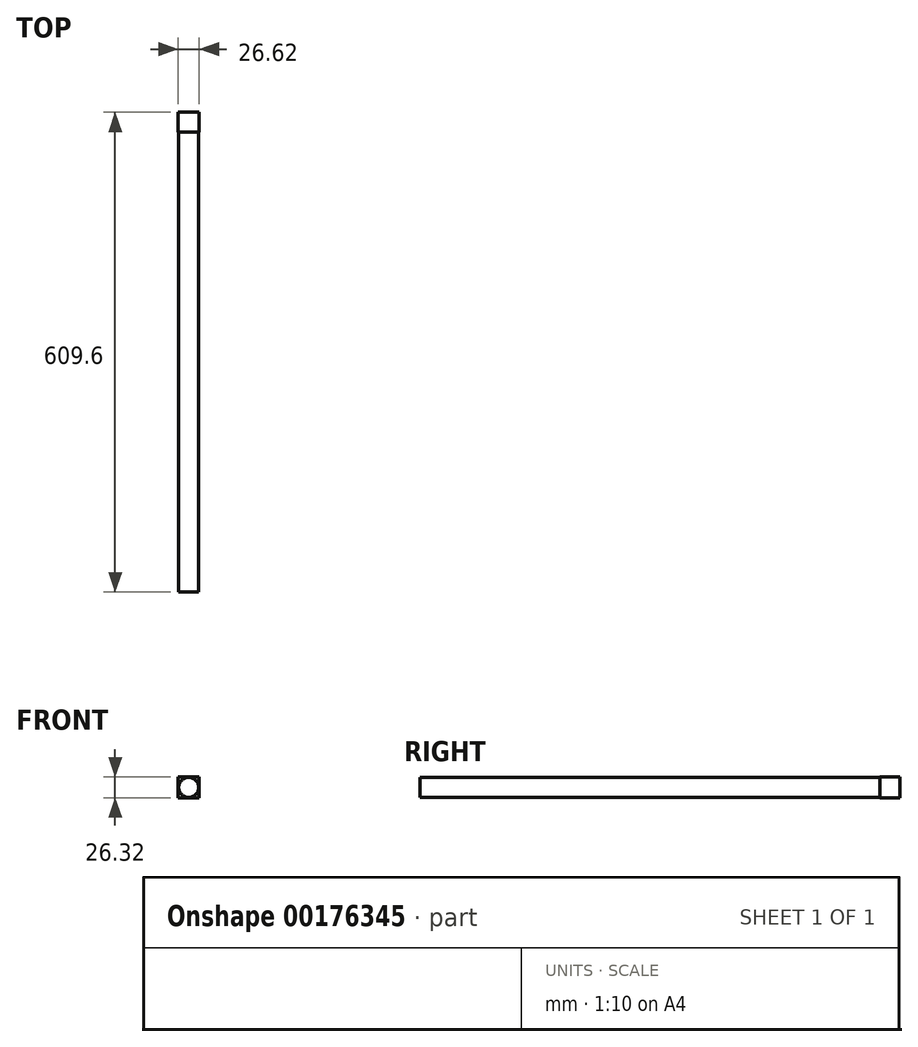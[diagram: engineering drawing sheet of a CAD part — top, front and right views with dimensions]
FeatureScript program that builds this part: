
annotation { "Feature Type Name" : "Feature", "Feature Type Description" : "" }
export const myFeature = defineFeature(function(context is Context, id is Id, definition is map)
    precondition{}
    {
        {
            var Q0;
            Q0=qCreatedBy(makeId("Front.planeOp"),FACE);
            var sketch = newSketch(context, id + "F0", { "sketchPlane" : qUnion([Q0])});
            skLineSegment(sketch, "E0.bottom", {"start": v(-13.3, 13.16) * mm, "end": v(13.3, 13.16) * mm});
            skLineSegment(sketch, "E0.top", {"start": v(-13.3, -13.16) * mm, "end": v(13.3, -13.16) * mm});
            skLineSegment(sketch, "E0.left", {"start": v(-13.3, 13.16) * mm, "end": v(-13.3, -13.16) * mm});
            skLineSegment(sketch, "E0.right", {"start": v(13.3, 13.16) * mm, "end": v(13.3, -13.16) * mm});
            skPoint(sketch, "E0.middle", {"position": v(0, 0) * mm});
            skCircle(sketch, "E1", {"center": v(0, 0) * mm, "radius": 12.7 * mm});
            skSolve(sketch);
        }
        {
            var Q0;
            Q0=makeQuery(id+"F0.imprint","IMPRINT",FACE,{"disambiguationData":[TD([[makeQuery(id+"F0.imprint","IMPRINT",EDGE,{"derivedFrom":sQuery(id+"F0.wireOp",EDGE,"E1")}),1.0]])]});
            extrude(context, id + "F1", {"entities" : qUnion([Q0]), "depth" : 584.2 * mm});
        }
        {
            var Q0;
            Q0=makeQuery(id+"F0.imprint","IMPRINT",FACE,{"disambiguationData":[TD([[makeQuery(id+"F0.imprint","IMPRINT",EDGE,{"derivedFrom":sQuery(id+"F0.wireOp",EDGE,"E1")}),1.0]])]});
            var Q1;
            Q1=makeQuery(id+"F0.imprint","IMPRINT",FACE,{"disambiguationData":[TD([[makeQuery(id+"F0.imprint","IMPRINT",EDGE,{"derivedFrom":sQuery(id+"F0.wireOp",EDGE,"E0.bottom")}),-1.0]])]});
            extrude(context, id + "F2", {"entities" : qUnion([Q0, Q1]), "operationType" : NewBodyOperationType.ADD, "oppositeDirection" : true, "depth" : 25.4 * mm});
        }
    });
